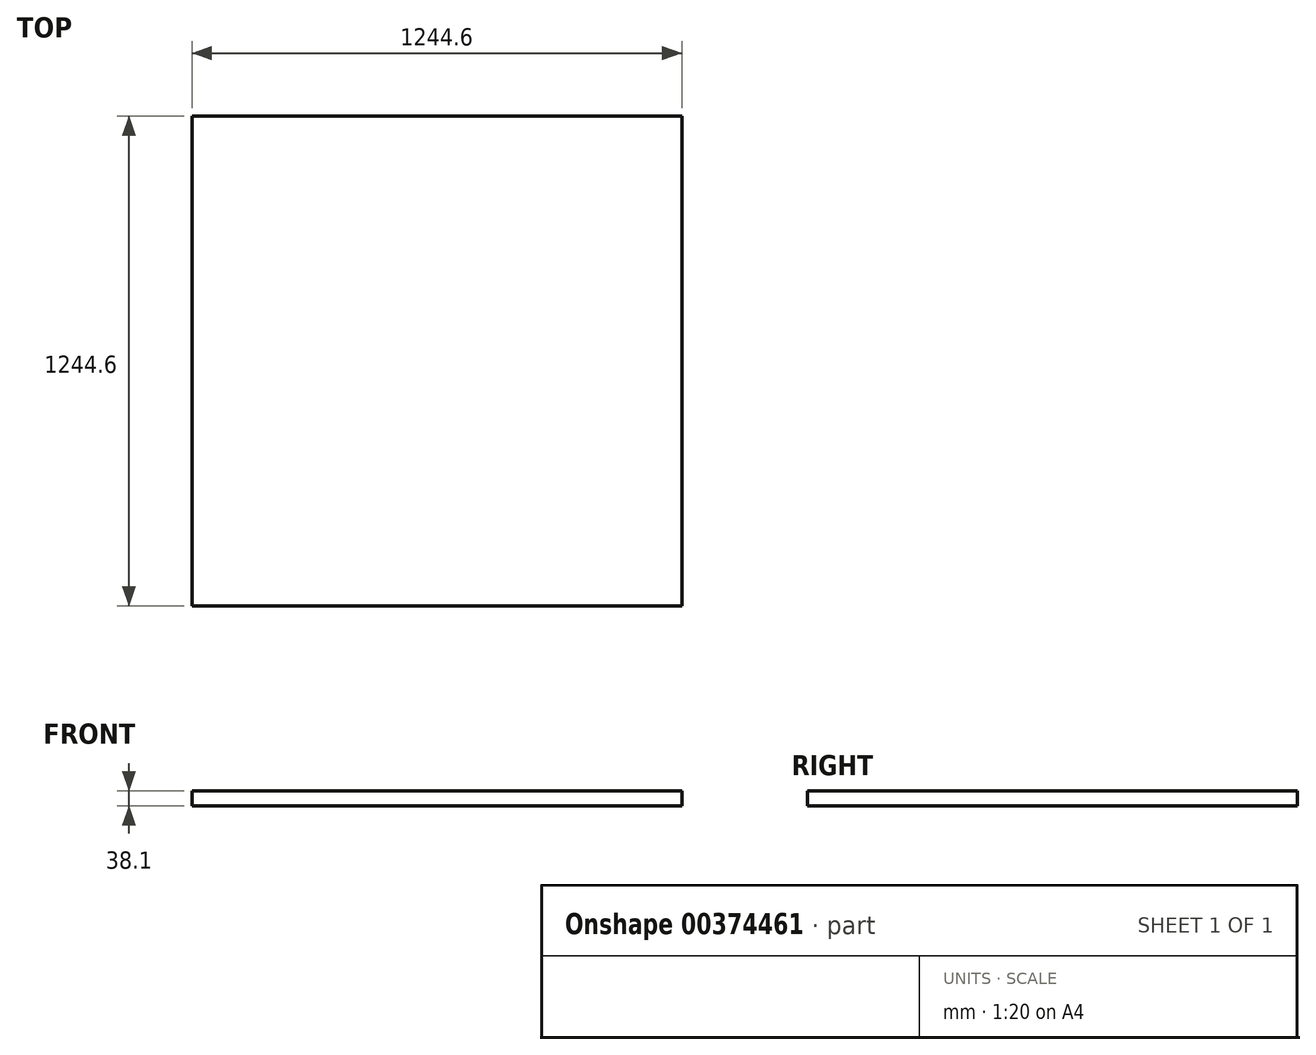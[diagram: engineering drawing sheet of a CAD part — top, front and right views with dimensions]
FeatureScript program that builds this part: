
annotation { "Feature Type Name" : "Feature", "Feature Type Description" : "" }
export const myFeature = defineFeature(function(context is Context, id is Id, definition is map)
    precondition{}
    {
        {
            var Q0;
            Q0=qCreatedBy(makeId("Front.planeOp"),FACE);
            var sketch = newSketch(context, id + "F0", { "sketchPlane" : qUnion([Q0])});
            skLineSegment(sketch, "E0.bottom", {"start": v(-613.91, -211.73) * mm, "end": v(630.69, -211.73) * mm});
            skLineSegment(sketch, "E0.top", {"start": v(-613.91, -173.63) * mm, "end": v(630.69, -173.63) * mm});
            skLineSegment(sketch, "E0.left", {"start": v(-613.91, -211.73) * mm, "end": v(-613.91, -173.63) * mm});
            skLineSegment(sketch, "E0.right", {"start": v(630.69, -211.73) * mm, "end": v(630.69, -173.63) * mm});
            skSolve(sketch);
        }
        {
            var Q0;
            Q0=makeQuery(id+"F0.imprint","IMPRINT",FACE,{"disambiguationData":[TD([[makeQuery(id+"F0.imprint","IMPRINT",EDGE,{"derivedFrom":sQuery(id+"F0.wireOp",EDGE,"E0.bottom")}),1.0]])]});
            extrude(context, id + "F1", {"entities" : qUnion([Q0]), "depth" : 1244.6 * mm});
        }
    });
